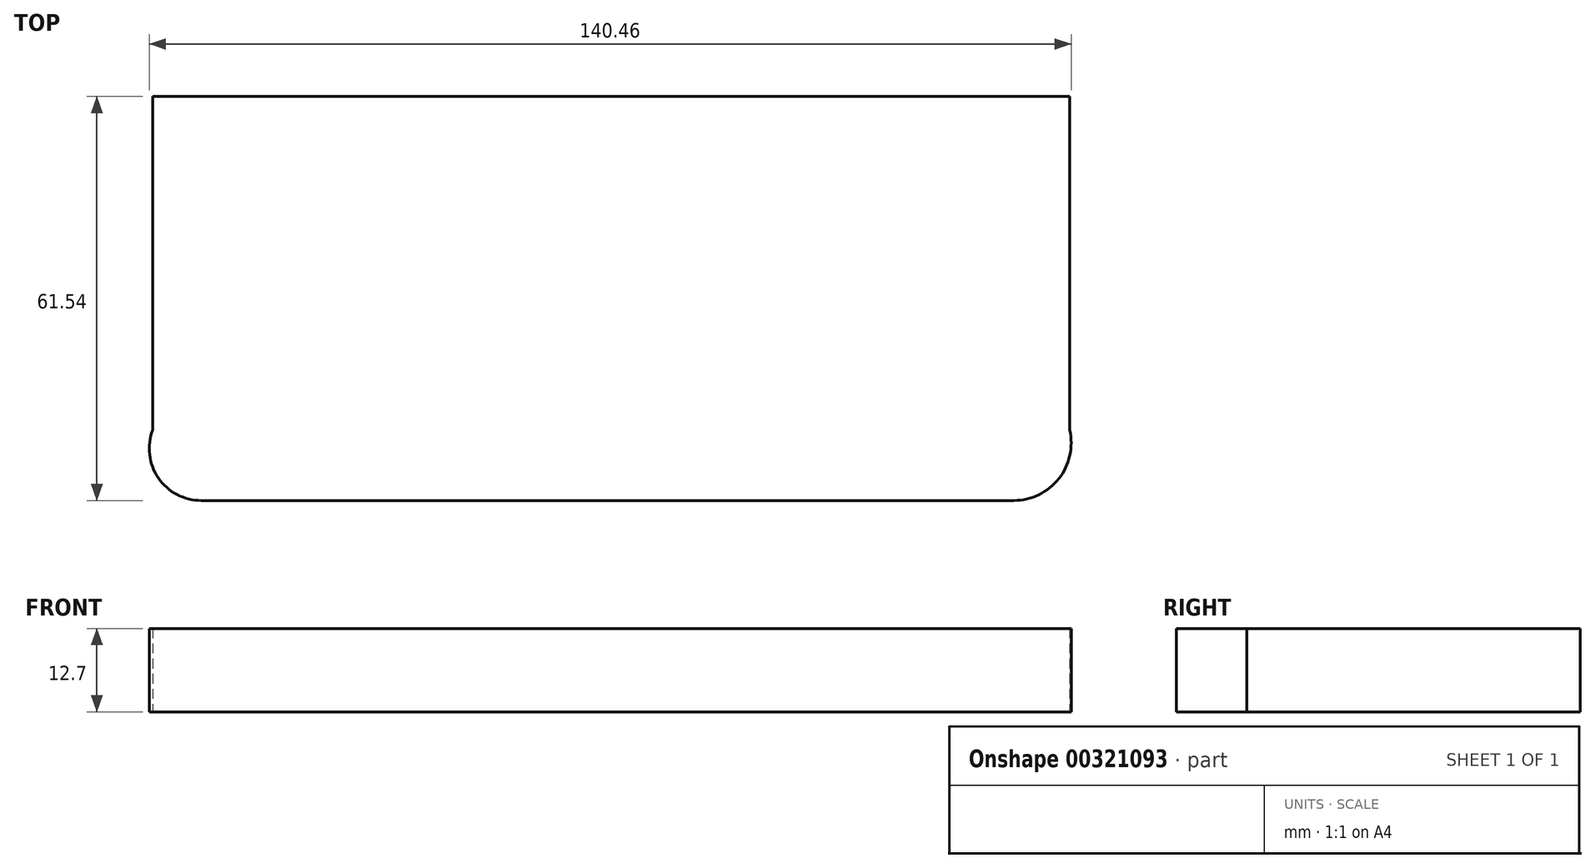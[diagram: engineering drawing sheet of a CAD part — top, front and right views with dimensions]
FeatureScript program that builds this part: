
annotation { "Feature Type Name" : "Feature", "Feature Type Description" : "" }
export const myFeature = defineFeature(function(context is Context, id is Id, definition is map)
    precondition{}
    {
        {
            var Q0;
            Q0=qCreatedBy(makeId("Top.planeOp"),FACE);
            var sketch = newSketch(context, id + "F0", { "sketchPlane" : qUnion([Q0])});
            skLineSegment(sketch, "E0", {"start": v(-42.46, -39.42) * mm, "end": v(81.35, -39.42) * mm});
            skArc(sketch, "E1", {"start": v(81.35, -39.42) * mm, "mid": v(88.2, -36.11) * mm, "end": v(89.85, -28.68) * mm});
            skArc(sketch, "E2", {"start": v(-49.85, -28.68) * mm, "mid": v(-48.98, -36) * mm, "end": v(-42.46, -39.42) * mm});
            skLineSegment(sketch, "E3", {"start": v(-49.85, -28.68) * mm, "end": v(-49.85, 22.12) * mm});
            skLineSegment(sketch, "E4", {"start": v(-49.85, 22.12) * mm, "end": v(89.85, 22.12) * mm});
            skLineSegment(sketch, "E5", {"start": v(89.85, 22.12) * mm, "end": v(89.85, -28.68) * mm});
            skSolve(sketch);
        }
        {
            var Q0;
            Q0 = qSketchRegion(id + "F0", true);
            extrude(context, id + "F1", {"entities" : qUnion([Q0]), "depth" : 12.7 * mm});
        }
    });
